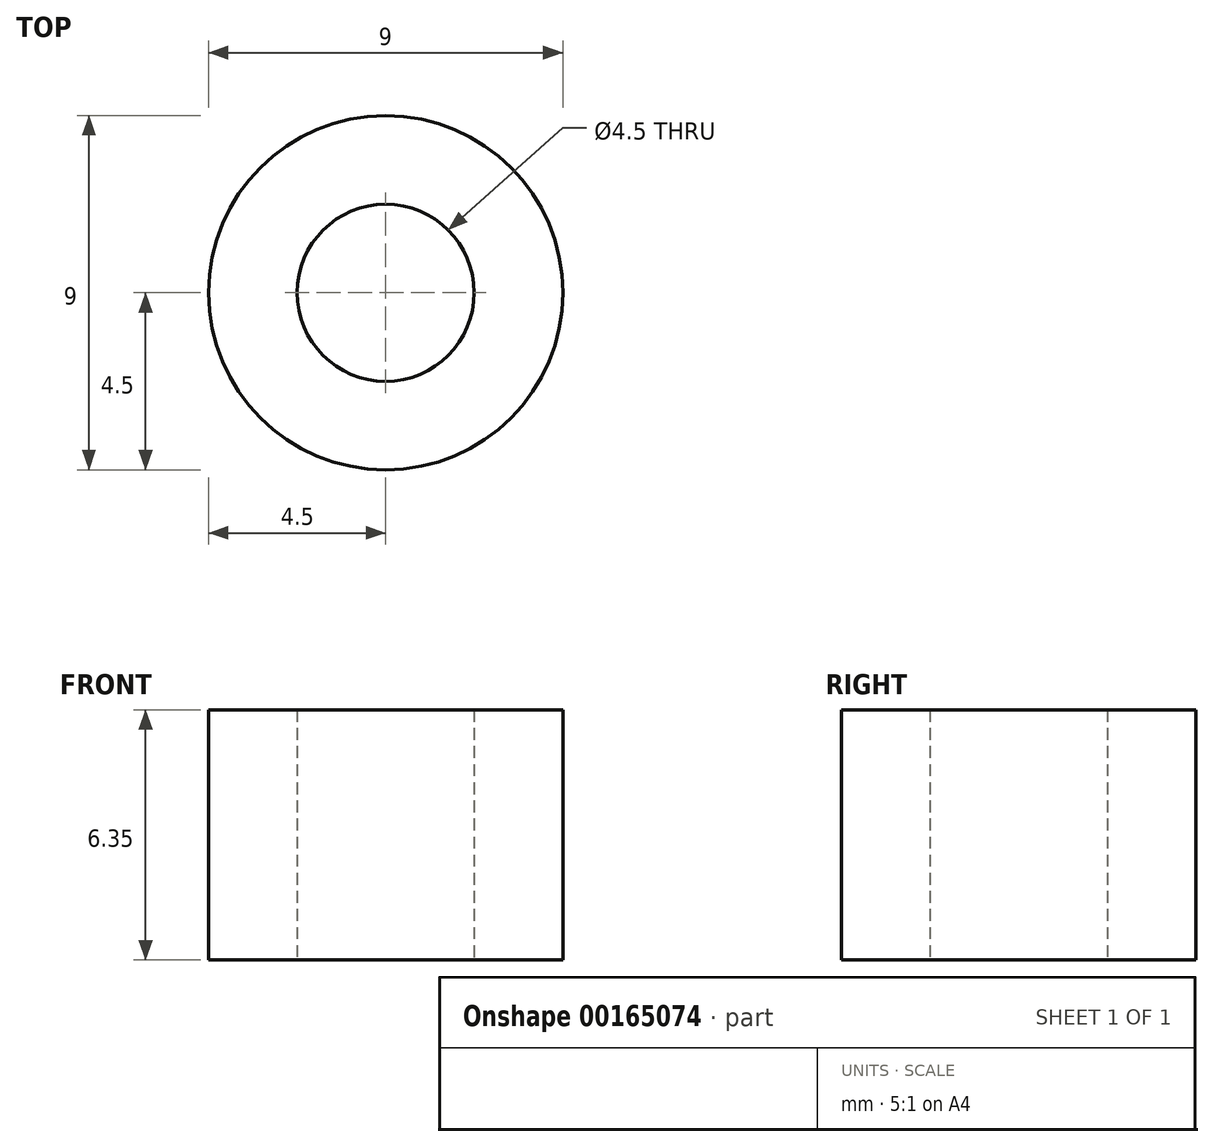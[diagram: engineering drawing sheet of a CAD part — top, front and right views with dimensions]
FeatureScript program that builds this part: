
annotation { "Feature Type Name" : "Feature", "Feature Type Description" : "" }
export const myFeature = defineFeature(function(context is Context, id is Id, definition is map)
    precondition{}
    {
        {
            var Q0;
            Q0=qCreatedBy(makeId("Top.planeOp"),FACE);
            var sketch = newSketch(context, id + "F0", { "sketchPlane" : qUnion([Q0])});
            skCircle(sketch, "E0", {"center": v(0, 0) * mm, "radius": 4.5 * mm});
            skCircle(sketch, "E1", {"center": v(0, 0) * mm, "radius": 2.25 * mm});
            skSolve(sketch);
        }
        {
            var Q0;
            Q0=makeQuery(id+"F0.imprint","IMPRINT",FACE,{"disambiguationData":[TD([[makeQuery(id+"F0.imprint","IMPRINT",EDGE,{"derivedFrom":sQuery(id+"F0.wireOp",EDGE,"E0")}),1.0]])]});
            extrude(context, id + "F1", {"entities" : qUnion([Q0]), "depth" : 6.35 * mm});
        }
    });
